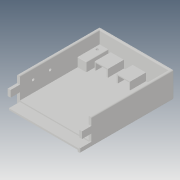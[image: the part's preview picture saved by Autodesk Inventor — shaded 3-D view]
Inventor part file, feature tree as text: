
AUTODESK INVENTOR PART (.ipt)
format: ipt  version: 2019 (Build 230136000, 136)  size: 403,456 bytes
history: native  units: mm
features: extrude x10, sketch x10, projected_geometry x5, other x4, fillet x2, plane x2, surface_op x1
ambient origin geometry x8: Origin, YZ Plane, XZ Plane, XY Plane, X Axis, Y Axis, Z Axis, Center Point
bodies: Solid1 (feature_tree)
feature tree (34):
  extrude  "Extrusion1"  Depth=170.0mm
  extrude  "Extrusion2"  Depth=5.0mm
  extrude  "Extrusion3"  Depth=25.0mm TaperAngle=0.0deg
  fillet  "Fillet1"  Radius=2.0mm
  extrude  "Extrusion4"  TaperAngle=0.0deg  [1 undecoded]
  extrude  "Extrusion5"  Depth=40.0mm
  fillet  "Fillet2"  [1 undecoded]
  plane  "Work Plane2"
  extrude  "Extrusion7"  Depth=35.0mm
  plane  "Work Plane1"
  extrude  "Extrusion8"  Depth=16.0mm TaperAngle=0.0deg
  surface_op  "Sculpt3"
  sketch  "Sketch8"  dims[d20=4.5mm d22=6.0mm]
  extrude  "Extrusion15"  Depth=6.0mm
  extrude  "Extrusion16"  Depth=7.0mm
  extrude  "Extrusion18"  Depth=1.0mm
  sketch  "Sketch1"  dims[d0=135.0mm d1=170.0mm]
  sketch  "Sketch2"  dims[d2=46.7mm d3=0.0mm d4=5.0mm]
  projected_geometry  "Projected Loop1"
  sketch  "Sketch3"  dims[d5=38.7mm d6=0.0mm d7=25.0mm d8=0.0mm d9=2.0mm]
  projected_geometry  "Projected Loop2"
  sketch  "Sketch4"  dims[d10=0.0mm d11=0.0mm]
  sketch  "Sketch5"  dims[d12=16.0mm d13=40.0mm d14=0.0mm]
  sketch  "Sketch6"  dims[d15=0.0mm d16=35.0mm]
  sketch  "Sketch7"  dims[d17=16.0mm d18=16.0mm d19=0.0mm]
  sketch  "Sketch14"  dims[d23=4.5mm d24=7.0mm]
  projected_geometry  "Projected Loop10"
  sketch  "Sketch16"  dims[d26=12.0mm d27=0.0mm d28=1.0mm d29=4.5mm d30=4.5mm d31=30.8mm d34=90.0mm d37=0.0mm d38=0.0mm d39=-1.5mm d40=7.5mm d41=7.5mm d42=3.15mm d43=0.0mm d44=10.0mm d45=12.5mm d46=18.0mm d51=20.0mm d70=1.75mm d91=12.0mm d92=8.0mm d93=2.05mm d94=2.05mm d95=20.0mm d96=29.0mm d97=0.0mm d98=0.8mm d99=0.8mm d100=1.8mm d101=4.4mm d102=0.0mm d105=1.8mm d106=4.4mm d107=0.0mm]
  projected_geometry  "Projected Loop13"
  projected_geometry  "Projected Loop14"
  other  "Composite3"
  other  "Srf3"
  other  "Assembly1"
  other  "Case_B1:1"
note: 2 required parameter values undecoded (feature->parameter linkage not recoverable at this tier; creation-order binding heuristic only, values carry confidence <= 0.55)
